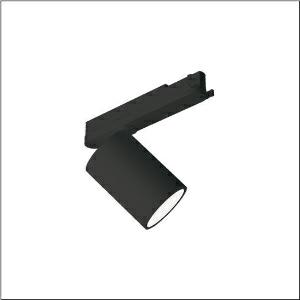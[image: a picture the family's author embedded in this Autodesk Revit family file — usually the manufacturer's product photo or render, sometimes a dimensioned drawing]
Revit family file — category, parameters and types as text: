
# Revit family: spot_31_51sf32mab4b
name_source: partatom
category: Lighting Fixtures
units: mm (PartAtom-declared; Revit-internal decimal feet)

## family parameters
Cut with Voids When Loaded = No
Host = Face
Light Source = No
Part Type = Normal
Room Calculation Point = No
Round Connector Dimension = Use Diameter
Shared = No

## types (1)
- --- (1 x LED, 4980 lm, 41.8 W, 3000K)
    Apparent Load = 42 VA
    CIE Flux Codes = 93 97 99 100 100
    Color Rendering = 90
    Color Temperature = 3000K
    Default Elevation = 1800 mm
    Description = Spot 31, directional spotlight, light control with lens, of PMMA, LED rated luminous flux: 4.790lm, light colour: 930, control gear: ECG Multilumen, with 3-phase adapter, mains connection: 220..240V, AC, 50/60Hz, of aluminium, jet black (RAL 9005), length: 213mm, diameter: 90mm, protection rating (complete): IP20, insulation class (complete): insulation class I (protective earthing), certification: CE, impact resistance: IK02, permissible ambient temperature for indoor applications: -20..+40°C, packaging unit: 1 piece
    Height = 175 mm
    Lamp = 1 x LED
    Lamp Light Flux = 4980 lm
    Lamp Power = 41.8 W
    Lamp count = 1
    Length = 90 mm
    Luminous efficacy = 119 lm/W
    Manufacturer = Siteco
    ModVariant = No
    Model = 51SF32MAB4B
    Mounting Place = Ceiling
    Mounting Type = Pendant
    Number of Poles = 1
    OnlyDefault = Yes
    Power Factor = 1
    Product Name = Spot 31
    Product group = directional spotlight
    ProductGroupID = 905
    Protection Class = Protection class I
    Protection Degree = IP 20
    RLX_Detail_Level = 1
    RLX_Emergency_Light_Flux = 0 lm
    RLX_Emergency_Type = 0
    RLX_Emergency_Type_DB = No
    RlxData = <blob elided: 20921 chars, md5=d6a743aa>
    Socket = socket
    Standby Power = 0 W
    System Light Flux = 4980 lm
    System Power = 42 W
    Type Comments = factory setting: luminous flux: 100 % | (ON | ON | ON | ON) | 1050 mA
    Type Image = l_1273723.jpg
    URL = http://relux.com
    VarID = @adj_078569
    Voltage = 0 V
    Weight = 0.00 kg
    Width = 0 mm  [stored 0 ft]

note: [stored X ft] marks values corroborated as IEEE doubles in the binary element streams (Revit-internal decimal feet)

## geometry (parser evidence)
native form markers: Blend x4, Sweep x11
no freeform markers — native parametric forms only
